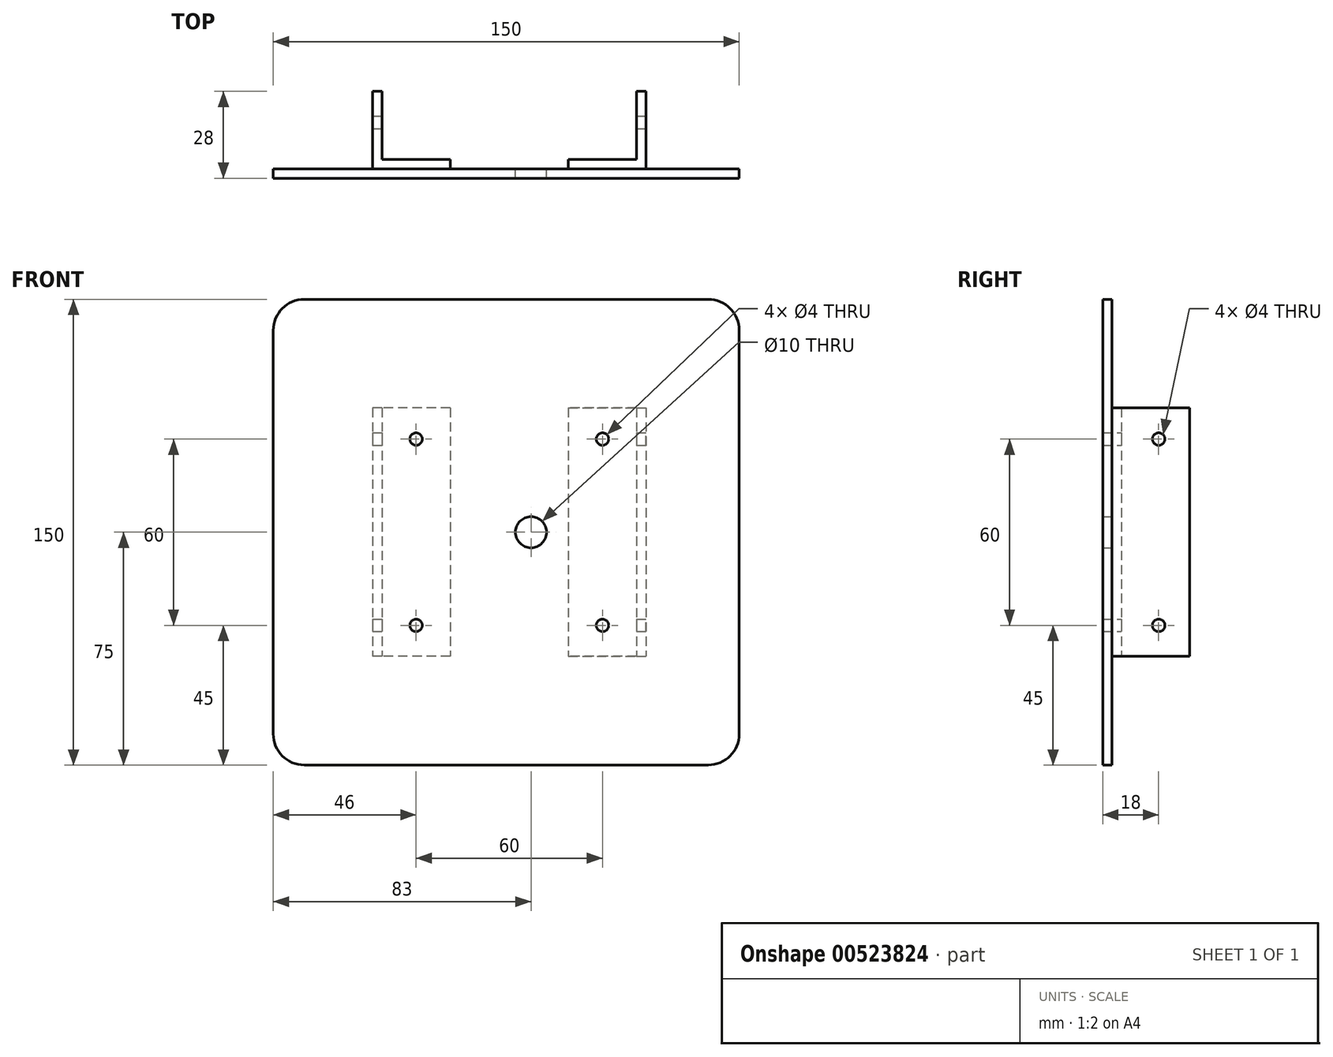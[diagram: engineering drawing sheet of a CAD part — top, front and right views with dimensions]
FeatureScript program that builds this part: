
annotation { "Feature Type Name" : "Feature", "Feature Type Description" : "" }
export const myFeature = defineFeature(function(context is Context, id is Id, definition is map)
    precondition{}
    {
        {
            var Q0;
            Q0=qCreatedBy(makeId("Front.planeOp"),FACE);
            var sketch = newSketch(context, id + "F0", { "sketchPlane" : qUnion([Q0])});
            skLineSegment(sketch, "E0.bottom", {"start": v(10, 0) * mm, "end": v(140, 0) * mm});
            skLineSegment(sketch, "E0.top", {"start": v(10, 150) * mm, "end": v(140, 150) * mm});
            skLineSegment(sketch, "E0.left", {"start": v(0, 10) * mm, "end": v(0, 140) * mm});
            skLineSegment(sketch, "E0.right", {"start": v(150, 10) * mm, "end": v(150, 140) * mm});
            skCircle(sketch, "E1", {"center": v(83, 75) * mm, "radius": 5 * mm});
            skPoint(sketch, "E2.visualSharp", {"position": v(0, 150) * mm});
            skArc(sketch, "E2.filletArc", {"start": v(10, 150) * mm, "mid": v(2.93, 147.07) * mm, "end": v(0, 140) * mm});
            skPoint(sketch, "E3.visualSharp", {"position": v(150, 150) * mm});
            skArc(sketch, "E3.filletArc", {"start": v(150, 140) * mm, "mid": v(147.07, 147.07) * mm, "end": v(140, 150) * mm});
            skPoint(sketch, "E4.visualSharp", {"position": v(0, 0) * mm});
            skArc(sketch, "E4.filletArc", {"start": v(0, 10) * mm, "mid": v(2.93, 2.93) * mm, "end": v(10, 0) * mm});
            skPoint(sketch, "E5.visualSharp", {"position": v(150, 0) * mm});
            skArc(sketch, "E5.filletArc", {"start": v(140, 0) * mm, "mid": v(147.07, 2.93) * mm, "end": v(150, 10) * mm});
            skLineSegment(sketch, "E6", {"start": v(83, 150) * mm, "end": v(83, 0) * mm, "construction": true});
            skSolve(sketch);
        }
        {
            var Q0;
            Q0=makeQuery(id+"F0.imprint","IMPRINT",FACE,{"disambiguationData":[TD([[makeQuery(id+"F0.imprint","IMPRINT",EDGE,{"derivedFrom":sQuery(id+"F0.wireOp",EDGE,"E0.bottom")}),1.0]])]});
            extrude(context, id + "F1", {"entities" : qUnion([Q0]), "depth" : 3 * mm, "offsetDistance" : 25 * mm});
        }
        {
            var Q0;
            Q0=makeQuery(id+"F1.opExtrude","CAP_FACE",FACE,{"disambiguationData":[OSD([sQuery(id+"F0.wireOp",EDGE,"E0.bottom"),sQuery(id+"F0.wireOp",EDGE,"E0.top"),sQuery(id+"F0.wireOp",EDGE,"E0.left"),sQuery(id+"F0.wireOp",EDGE,"E0.right"),sQuery(id+"F0.wireOp",EDGE,"E1"),sQuery(id+"F0.wireOp",EDGE,"E2.filletArc"),sQuery(id+"F0.wireOp",EDGE,"E3.filletArc"),sQuery(id+"F0.wireOp",EDGE,"E4.filletArc"),sQuery(id+"F0.wireOp",EDGE,"E5.filletArc")])],"isStart":true});
            var sketch = newSketch(context, id + "F2", { "sketchPlane" : qUnion([Q0])});
            skLineSegment(sketch, "E7.bottom", {"start": v(-117, 115) * mm, "end": v(-95, 115) * mm});
            skLineSegment(sketch, "E7.top", {"start": v(-117, 35) * mm, "end": v(-95, 35) * mm});
            skLineSegment(sketch, "E7.left", {"start": v(-117, 115) * mm, "end": v(-117, 35) * mm});
            skLineSegment(sketch, "E7.right", {"start": v(-95, 115) * mm, "end": v(-95, 35) * mm});
            skLineSegment(sketch, "E8.bottom", {"start": v(-57, 115) * mm, "end": v(-35, 115) * mm});
            skLineSegment(sketch, "E8.top", {"start": v(-57, 35) * mm, "end": v(-35, 35) * mm});
            skLineSegment(sketch, "E8.left", {"start": v(-57, 115) * mm, "end": v(-57, 35) * mm});
            skLineSegment(sketch, "E8.right", {"start": v(-35, 115) * mm, "end": v(-35, 35) * mm});
            skLineSegment(sketch, "E9.bottom", {"start": v(-117, 115) * mm, "end": v(-120, 115) * mm});
            skLineSegment(sketch, "E9.top", {"start": v(-117, 35) * mm, "end": v(-120, 35) * mm});
            skLineSegment(sketch, "E9.right", {"start": v(-120, 115) * mm, "end": v(-120, 35) * mm});
            skLineSegment(sketch, "E10.bottom", {"start": v(-35, 115) * mm, "end": v(-32, 115) * mm});
            skLineSegment(sketch, "E10.top", {"start": v(-35, 35) * mm, "end": v(-32, 35) * mm});
            skLineSegment(sketch, "E10.right", {"start": v(-32, 115) * mm, "end": v(-32, 35) * mm});
            skSolve(sketch);
        }
        {
            var Q0;
            Q0=makeQuery(id+"F2.imprint","IMPRINT",FACE,{"disambiguationData":[TD([[makeQuery(id+"F2.imprint","IMPRINT",EDGE,{"derivedFrom":sQuery(id+"F2.wireOp",EDGE,"E9.bottom")}),1.0]])]});
            var Q1;
            Q1=makeQuery(id+"F2.imprint","IMPRINT",FACE,{"disambiguationData":[TD([[makeQuery(id+"F2.imprint","IMPRINT",EDGE,{"derivedFrom":sQuery(id+"F2.wireOp",EDGE,"E10.bottom")}),-1.0]])]});
            extrude(context, id + "F3", {"entities" : qUnion([Q0, Q1]), "operationType" : NewBodyOperationType.ADD, "depth" : 25 * mm, "offsetDistance" : 25 * mm});
        }
        {
            var Q0;
            Q0 = qSketchRegion(id + "F2", true);
            extrude(context, id + "F4", {"entities" : qUnion([Q0]), "operationType" : NewBodyOperationType.ADD, "depth" : 3 * mm, "offsetDistance" : 25 * mm});
        }
        {
            var Q0;
            Q0=makeQuery(id+"F3.opExtrude","SWEPT_FACE",FACE,{"disambiguationData":[OSD([sQuery(id+"F2.wireOp",EDGE,"E9.right")])]});
            var sketch = newSketch(context, id + "F5", { "sketchPlane" : qUnion([Q0])});
            skCircle(sketch, "E11", {"center": v(15, 105) * mm, "radius": 2 * mm});
            skCircle(sketch, "E12", {"center": v(15, 45) * mm, "radius": 2 * mm});
            skLineSegment(sketch, "E13", {"start": v(15, 115) * mm, "end": v(15, 75) * mm, "construction": true});
            skLineSegment(sketch, "E14", {"start": v(15, 75) * mm, "end": v(15, 35) * mm, "construction": true});
            skLineSegment(sketch, "E15", {"start": v(15, 105) * mm, "end": v(15, 75) * mm, "construction": true});
            skLineSegment(sketch, "E16", {"start": v(15, 75) * mm, "end": v(15, 45) * mm, "construction": true});
            skSolve(sketch);
        }
        {
            var Q0;
            Q0 = qSketchRegion(id + "F5", true);
            extrude(context, id + "F6", {"entities" : qUnion([Q0]), "operationType" : NewBodyOperationType.REMOVE, "oppositeDirection" : true, "depth" : 150 * mm, "offsetDistance" : 25 * mm});
        }
        {
            var Q0;
            Q0=makeQuery(id+"F4.opExtrude","CAP_FACE",FACE,{"disambiguationData":[OSD([sQuery(id+"F2.wireOp",EDGE,"E8.bottom"),sQuery(id+"F2.wireOp",EDGE,"E8.top"),sQuery(id+"F2.wireOp",EDGE,"E8.left"),sQuery(id+"F2.wireOp",EDGE,"E10.bottom"),sQuery(id+"F2.wireOp",EDGE,"E10.top"),sQuery(id+"F2.wireOp",EDGE,"E10.right")])],"isStart":false});
            var sketch = newSketch(context, id + "F7", { "sketchPlane" : qUnion([Q0])});
            skCircle(sketch, "E17", {"center": v(-46, 45) * mm, "radius": 2 * mm});
            skCircle(sketch, "E18", {"center": v(-46, 105) * mm, "radius": 2 * mm});
            skLineSegment(sketch, "E19", {"start": v(-46, 35) * mm, "end": v(-46, 75) * mm, "construction": true});
            skLineSegment(sketch, "E20", {"start": v(-46, 75) * mm, "end": v(-46, 115) * mm, "construction": true});
            skLineSegment(sketch, "E21", {"start": v(-46, 45) * mm, "end": v(-46, 75) * mm, "construction": true});
            skLineSegment(sketch, "E22", {"start": v(-46, 75) * mm, "end": v(-46, 105) * mm, "construction": true});
            skCircle(sketch, "E23", {"center": v(-106, 45) * mm, "radius": 2 * mm});
            skCircle(sketch, "E24", {"center": v(-106, 105) * mm, "radius": 2 * mm});
            skSolve(sketch);
        }
        {
            var Q0;
            Q0 = qSketchRegion(id + "F7", true);
            extrude(context, id + "F8", {"entities" : qUnion([Q0]), "operationType" : NewBodyOperationType.REMOVE, "oppositeDirection" : true, "depth" : 25 * mm, "offsetDistance" : 25 * mm});
        }
    });
